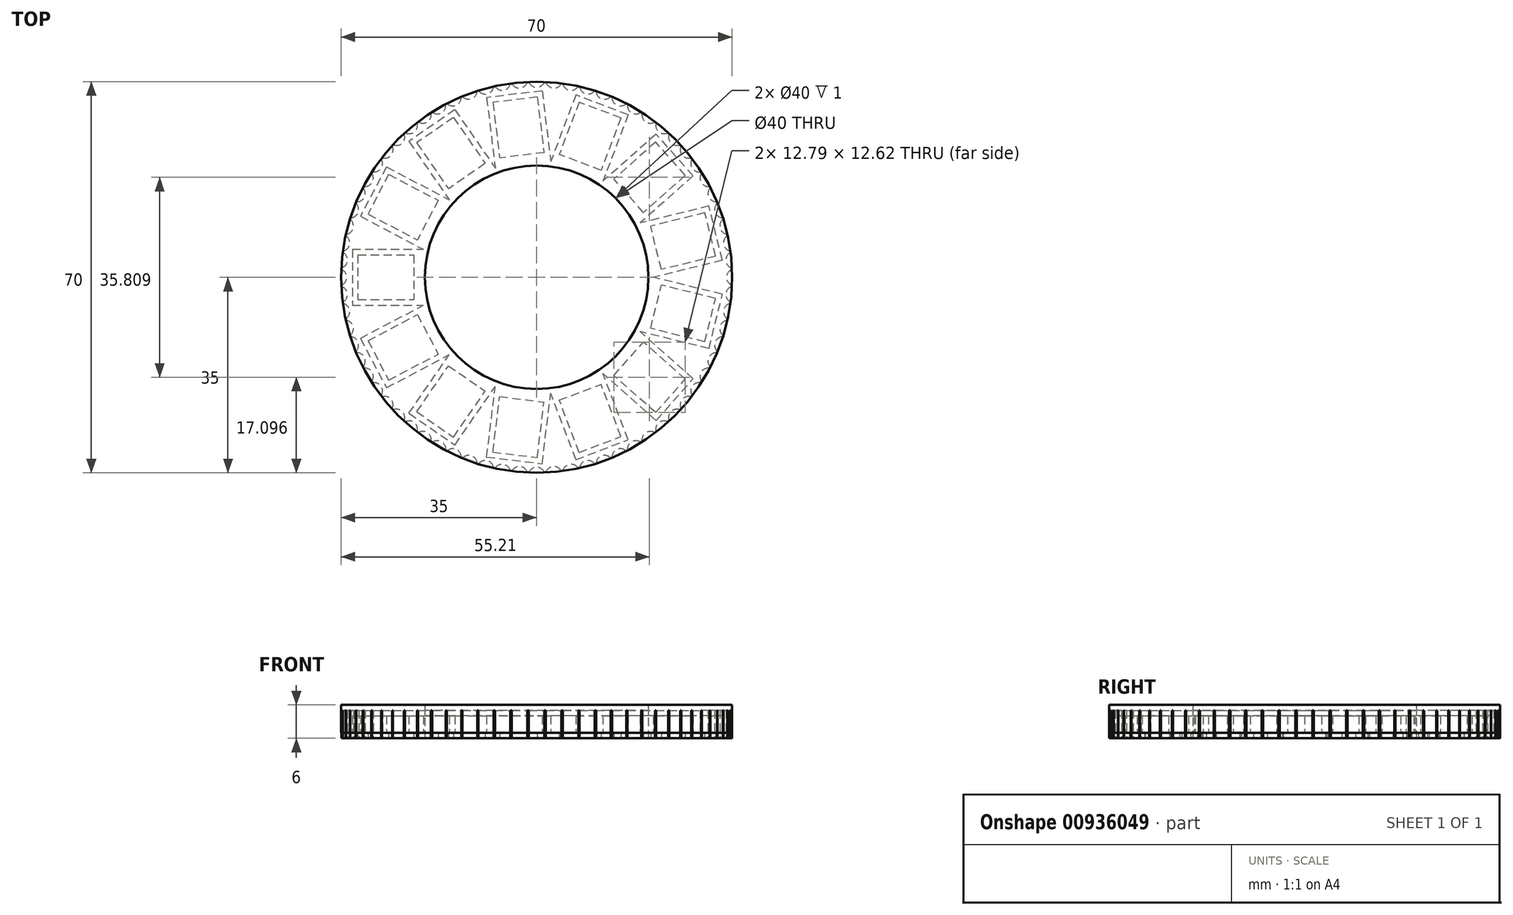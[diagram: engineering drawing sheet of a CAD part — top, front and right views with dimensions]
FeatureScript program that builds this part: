
annotation { "Feature Type Name" : "Feature", "Feature Type Description" : "" }
export const myFeature = defineFeature(function(context is Context, id is Id, definition is map)
    precondition{}
    {
        {
            var Q0;
            Q0=qCreatedBy(makeId("Top.planeOp"),FACE);
            var sketch = newSketch(context, id + "F0", { "sketchPlane" : qUnion([Q0])});
            skLineSegment(sketch, "E0.bottom", {"start": v(-32, 4) * mm, "end": v(-22, 4) * mm});
            skLineSegment(sketch, "E0.top", {"start": v(-32, -4) * mm, "end": v(-22, -4) * mm});
            skLineSegment(sketch, "E0.left", {"start": v(-32, 4) * mm, "end": v(-32, -4) * mm});
            skLineSegment(sketch, "E0.right", {"start": v(-22, 4) * mm, "end": v(-22, -4) * mm});
            skLineSegment(sketch, "E1", {"start": v(0, 0) * mm, "end": v(-43.95, 0) * mm, "construction": true});
            skLineSegment(sketch, "E2.bottom", {"start": v(-33, 5) * mm, "end": v(0, 5) * mm});
            skLineSegment(sketch, "E2.top", {"start": v(-33, -5) * mm, "end": v(0, -5) * mm});
            skLineSegment(sketch, "E2.left", {"start": v(-33, 5) * mm, "end": v(-33, -5) * mm});
            skLineSegment(sketch, "E2.right", {"start": v(0, 5) * mm, "end": v(0, -5) * mm});
            skLineSegment(sketch, "E3.1.0", {"start": v(-30.2, -11.33) * mm, "end": v(-21.34, -6.68) * mm});
            skLineSegment(sketch, "E3.1.1", {"start": v(-26.48, -18.41) * mm, "end": v(-17.62, -13.77) * mm});
            skLineSegment(sketch, "E3.1.2", {"start": v(-30.2, -11.33) * mm, "end": v(-26.48, -18.41) * mm});
            skLineSegment(sketch, "E3.1.3", {"start": v(-31.54, -10.9) * mm, "end": v(-2.32, 4.43) * mm});
            skLineSegment(sketch, "E3.1.4", {"start": v(-21.34, -6.68) * mm, "end": v(-17.62, -13.77) * mm});
            skLineSegment(sketch, "E3.1.5", {"start": v(-26.9, -19.76) * mm, "end": v(2.32, -4.43) * mm});
            skLineSegment(sketch, "E3.1.6", {"start": v(-31.54, -10.9) * mm, "end": v(-26.9, -19.76) * mm});
            skLineSegment(sketch, "E3.1.7", {"start": v(-2.32, 4.43) * mm, "end": v(2.32, -4.43) * mm});
            skLineSegment(sketch, "E3.1.8", {"start": v(0, 0) * mm, "end": v(-38.92, -20.43) * mm, "construction": true});
            skLineSegment(sketch, "E3.2.0", {"start": v(-21.47, -24.06) * mm, "end": v(-15.79, -15.83) * mm});
            skLineSegment(sketch, "E3.2.1", {"start": v(-14.89, -28.6) * mm, "end": v(-9.2, -20.38) * mm});
            skLineSegment(sketch, "E3.2.2", {"start": v(-21.47, -24.06) * mm, "end": v(-14.89, -28.6) * mm});
            skLineSegment(sketch, "E3.2.3", {"start": v(-22.86, -24.32) * mm, "end": v(-4.11, 2.84) * mm});
            skLineSegment(sketch, "E3.2.4", {"start": v(-15.79, -15.83) * mm, "end": v(-9.2, -20.38) * mm});
            skLineSegment(sketch, "E3.2.5", {"start": v(-14.63, -30) * mm, "end": v(4.11, -2.84) * mm});
            skLineSegment(sketch, "E3.2.6", {"start": v(-22.86, -24.32) * mm, "end": v(-14.63, -30) * mm});
            skLineSegment(sketch, "E3.2.7", {"start": v(-4.11, 2.84) * mm, "end": v(4.11, -2.84) * mm});
            skLineSegment(sketch, "E3.2.8", {"start": v(0, 0) * mm, "end": v(-24.97, -36.17) * mm, "construction": true});
            skLineSegment(sketch, "E3.3.0", {"start": v(-7.83, -31.28) * mm, "end": v(-6.62, -21.36) * mm});
            skLineSegment(sketch, "E3.3.1", {"start": v(0.11, -32.25) * mm, "end": v(1.32, -22.32) * mm});
            skLineSegment(sketch, "E3.3.2", {"start": v(-7.83, -31.28) * mm, "end": v(0.11, -32.25) * mm});
            skLineSegment(sketch, "E3.3.3", {"start": v(-8.94, -32.16) * mm, "end": v(-4.96, 0.6) * mm});
            skLineSegment(sketch, "E3.3.4", {"start": v(-6.62, -21.36) * mm, "end": v(1.32, -22.32) * mm});
            skLineSegment(sketch, "E3.3.5", {"start": v(0.99, -33.36) * mm, "end": v(4.96, -0.6) * mm});
            skLineSegment(sketch, "E3.3.6", {"start": v(-8.94, -32.16) * mm, "end": v(0.99, -33.36) * mm});
            skLineSegment(sketch, "E3.3.7", {"start": v(-4.96, 0.6) * mm, "end": v(4.96, -0.6) * mm});
            skLineSegment(sketch, "E3.3.8", {"start": v(0, 0) * mm, "end": v(-5.3, -43.63) * mm, "construction": true});
            skLineSegment(sketch, "E3.4.0", {"start": v(7.6, -31.34) * mm, "end": v(4.06, -21.99) * mm});
            skLineSegment(sketch, "E3.4.1", {"start": v(15.09, -28.5) * mm, "end": v(11.54, -19.15) * mm});
            skLineSegment(sketch, "E3.4.2", {"start": v(7.6, -31.34) * mm, "end": v(15.09, -28.5) * mm});
            skLineSegment(sketch, "E3.4.3", {"start": v(7.03, -32.63) * mm, "end": v(-4.68, -1.77) * mm});
            skLineSegment(sketch, "E3.4.4", {"start": v(4.06, -21.99) * mm, "end": v(11.54, -19.15) * mm});
            skLineSegment(sketch, "E3.4.5", {"start": v(16.38, -29.08) * mm, "end": v(4.68, 1.77) * mm});
            skLineSegment(sketch, "E3.4.6", {"start": v(7.03, -32.63) * mm, "end": v(16.38, -29.08) * mm});
            skLineSegment(sketch, "E3.4.7", {"start": v(-4.68, -1.77) * mm, "end": v(4.68, 1.77) * mm});
            skLineSegment(sketch, "E3.4.8", {"start": v(0, 0) * mm, "end": v(15.59, -41.1) * mm, "construction": true});
            skLineSegment(sketch, "E3.5.0", {"start": v(21.3, -24.21) * mm, "end": v(13.81, -17.58) * mm});
            skLineSegment(sketch, "E3.5.1", {"start": v(26.6, -18.23) * mm, "end": v(19.12, -11.6) * mm});
            skLineSegment(sketch, "E3.5.2", {"start": v(21.3, -24.21) * mm, "end": v(26.6, -18.23) * mm});
            skLineSegment(sketch, "E3.5.3", {"start": v(21.39, -25.63) * mm, "end": v(-3.32, -3.74) * mm});
            skLineSegment(sketch, "E3.5.4", {"start": v(13.81, -17.58) * mm, "end": v(19.12, -11.6) * mm});
            skLineSegment(sketch, "E3.5.5", {"start": v(28.02, -18.14) * mm, "end": v(3.32, 3.74) * mm});
            skLineSegment(sketch, "E3.5.6", {"start": v(21.39, -25.63) * mm, "end": v(28.02, -18.14) * mm});
            skLineSegment(sketch, "E3.5.7", {"start": v(-3.32, -3.74) * mm, "end": v(3.32, 3.74) * mm});
            skLineSegment(sketch, "E3.5.8", {"start": v(0, 0) * mm, "end": v(32.9, -29.15) * mm, "construction": true});
            skLineSegment(sketch, "E3.6.0", {"start": v(30.11, -11.54) * mm, "end": v(20.4, -9.15) * mm});
            skLineSegment(sketch, "E3.6.1", {"start": v(32.03, -3.77) * mm, "end": v(22.32, -1.38) * mm});
            skLineSegment(sketch, "E3.6.2", {"start": v(30.11, -11.54) * mm, "end": v(32.03, -3.77) * mm});
            skLineSegment(sketch, "E3.6.3", {"start": v(30.84, -12.75) * mm, "end": v(-1.2, -4.85) * mm});
            skLineSegment(sketch, "E3.6.4", {"start": v(20.4, -9.15) * mm, "end": v(22.32, -1.38) * mm});
            skLineSegment(sketch, "E3.6.5", {"start": v(33.24, -3.04) * mm, "end": v(1.2, 4.85) * mm});
            skLineSegment(sketch, "E3.6.6", {"start": v(30.84, -12.75) * mm, "end": v(33.24, -3.04) * mm});
            skLineSegment(sketch, "E3.6.7", {"start": v(-1.2, -4.85) * mm, "end": v(1.2, 4.85) * mm});
            skLineSegment(sketch, "E3.6.8", {"start": v(0, 0) * mm, "end": v(42.68, -10.52) * mm, "construction": true});
            skLineSegment(sketch, "E3.7.0", {"start": v(32.03, 3.77) * mm, "end": v(22.32, 1.38) * mm});
            skLineSegment(sketch, "E3.7.1", {"start": v(30.11, 11.54) * mm, "end": v(20.4, 9.15) * mm});
            skLineSegment(sketch, "E3.7.2", {"start": v(32.03, 3.77) * mm, "end": v(30.11, 11.54) * mm});
            skLineSegment(sketch, "E3.7.3", {"start": v(33.24, 3.04) * mm, "end": v(1.2, -4.85) * mm});
            skLineSegment(sketch, "E3.7.4", {"start": v(22.32, 1.38) * mm, "end": v(20.4, 9.15) * mm});
            skLineSegment(sketch, "E3.7.5", {"start": v(30.84, 12.75) * mm, "end": v(-1.2, 4.85) * mm});
            skLineSegment(sketch, "E3.7.6", {"start": v(33.24, 3.04) * mm, "end": v(30.84, 12.75) * mm});
            skLineSegment(sketch, "E3.7.7", {"start": v(1.2, -4.85) * mm, "end": v(-1.2, 4.85) * mm});
            skLineSegment(sketch, "E3.7.8", {"start": v(0, 0) * mm, "end": v(42.68, 10.52) * mm, "construction": true});
            skLineSegment(sketch, "E3.8.0", {"start": v(26.6, 18.23) * mm, "end": v(19.12, 11.6) * mm});
            skLineSegment(sketch, "E3.8.1", {"start": v(21.3, 24.21) * mm, "end": v(13.81, 17.58) * mm});
            skLineSegment(sketch, "E3.8.2", {"start": v(26.6, 18.23) * mm, "end": v(21.3, 24.21) * mm});
            skLineSegment(sketch, "E3.8.3", {"start": v(28.02, 18.14) * mm, "end": v(3.32, -3.74) * mm});
            skLineSegment(sketch, "E3.8.4", {"start": v(19.12, 11.6) * mm, "end": v(13.81, 17.58) * mm});
            skLineSegment(sketch, "E3.8.5", {"start": v(21.39, 25.63) * mm, "end": v(-3.32, 3.74) * mm});
            skLineSegment(sketch, "E3.8.6", {"start": v(28.02, 18.14) * mm, "end": v(21.39, 25.63) * mm});
            skLineSegment(sketch, "E3.8.7", {"start": v(3.32, -3.74) * mm, "end": v(-3.32, 3.74) * mm});
            skLineSegment(sketch, "E3.8.8", {"start": v(0, 0) * mm, "end": v(32.9, 29.15) * mm, "construction": true});
            skLineSegment(sketch, "E3.9.0", {"start": v(15.09, 28.5) * mm, "end": v(11.54, 19.15) * mm});
            skLineSegment(sketch, "E3.9.1", {"start": v(7.6, 31.34) * mm, "end": v(4.06, 21.99) * mm});
            skLineSegment(sketch, "E3.9.2", {"start": v(15.09, 28.5) * mm, "end": v(7.6, 31.34) * mm});
            skLineSegment(sketch, "E3.9.3", {"start": v(16.38, 29.08) * mm, "end": v(4.68, -1.77) * mm});
            skLineSegment(sketch, "E3.9.4", {"start": v(11.54, 19.15) * mm, "end": v(4.06, 21.99) * mm});
            skLineSegment(sketch, "E3.9.5", {"start": v(7.03, 32.63) * mm, "end": v(-4.68, 1.77) * mm});
            skLineSegment(sketch, "E3.9.6", {"start": v(16.38, 29.08) * mm, "end": v(7.03, 32.63) * mm});
            skLineSegment(sketch, "E3.9.7", {"start": v(4.68, -1.77) * mm, "end": v(-4.68, 1.77) * mm});
            skLineSegment(sketch, "E3.9.8", {"start": v(0, 0) * mm, "end": v(15.59, 41.1) * mm, "construction": true});
            skLineSegment(sketch, "E3.10.0", {"start": v(0.11, 32.25) * mm, "end": v(1.32, 22.32) * mm});
            skLineSegment(sketch, "E3.10.1", {"start": v(-7.83, 31.28) * mm, "end": v(-6.62, 21.36) * mm});
            skLineSegment(sketch, "E3.10.2", {"start": v(0.11, 32.25) * mm, "end": v(-7.83, 31.28) * mm});
            skLineSegment(sketch, "E3.10.3", {"start": v(0.99, 33.36) * mm, "end": v(4.96, 0.6) * mm});
            skLineSegment(sketch, "E3.10.4", {"start": v(1.32, 22.32) * mm, "end": v(-6.62, 21.36) * mm});
            skLineSegment(sketch, "E3.10.5", {"start": v(-8.94, 32.16) * mm, "end": v(-4.96, -0.6) * mm});
            skLineSegment(sketch, "E3.10.6", {"start": v(0.99, 33.36) * mm, "end": v(-8.94, 32.16) * mm});
            skLineSegment(sketch, "E3.10.7", {"start": v(4.96, 0.6) * mm, "end": v(-4.96, -0.6) * mm});
            skLineSegment(sketch, "E3.10.8", {"start": v(0, 0) * mm, "end": v(-5.3, 43.63) * mm, "construction": true});
            skLineSegment(sketch, "E3.11.0", {"start": v(-14.89, 28.6) * mm, "end": v(-9.2, 20.38) * mm});
            skLineSegment(sketch, "E3.11.1", {"start": v(-21.47, 24.06) * mm, "end": v(-15.79, 15.83) * mm});
            skLineSegment(sketch, "E3.11.2", {"start": v(-14.89, 28.6) * mm, "end": v(-21.47, 24.06) * mm});
            skLineSegment(sketch, "E3.11.3", {"start": v(-14.63, 30) * mm, "end": v(4.11, 2.84) * mm});
            skLineSegment(sketch, "E3.11.4", {"start": v(-9.2, 20.38) * mm, "end": v(-15.79, 15.83) * mm});
            skLineSegment(sketch, "E3.11.5", {"start": v(-22.86, 24.32) * mm, "end": v(-4.11, -2.84) * mm});
            skLineSegment(sketch, "E3.11.6", {"start": v(-14.63, 30) * mm, "end": v(-22.86, 24.32) * mm});
            skLineSegment(sketch, "E3.11.7", {"start": v(4.11, 2.84) * mm, "end": v(-4.11, -2.84) * mm});
            skLineSegment(sketch, "E3.11.8", {"start": v(0, 0) * mm, "end": v(-24.97, 36.17) * mm, "construction": true});
            skLineSegment(sketch, "E3.12.0", {"start": v(-26.48, 18.41) * mm, "end": v(-17.62, 13.77) * mm});
            skLineSegment(sketch, "E3.12.1", {"start": v(-30.2, 11.33) * mm, "end": v(-21.34, 6.68) * mm});
            skLineSegment(sketch, "E3.12.2", {"start": v(-26.48, 18.41) * mm, "end": v(-30.2, 11.33) * mm});
            skLineSegment(sketch, "E3.12.3", {"start": v(-26.9, 19.76) * mm, "end": v(2.32, 4.43) * mm});
            skLineSegment(sketch, "E3.12.4", {"start": v(-17.62, 13.77) * mm, "end": v(-21.34, 6.68) * mm});
            skLineSegment(sketch, "E3.12.5", {"start": v(-31.54, 10.9) * mm, "end": v(-2.32, -4.43) * mm});
            skLineSegment(sketch, "E3.12.6", {"start": v(-26.9, 19.76) * mm, "end": v(-31.54, 10.9) * mm});
            skLineSegment(sketch, "E3.12.7", {"start": v(2.32, 4.43) * mm, "end": v(-2.32, -4.43) * mm});
            skLineSegment(sketch, "E3.12.8", {"start": v(0, 0) * mm, "end": v(-38.92, 20.43) * mm, "construction": true});
            skPoint(sketch, "E3.center", {"position": v(0, 0) * mm});
            skSolve(sketch);
        }
        {
            var Q0;
            Q0=qCreatedBy(makeId("Top.planeOp"),FACE);
            var sketch = newSketch(context, id + "F1", { "sketchPlane" : qUnion([Q0])});
            skCircle(sketch, "E4", {"center": v(0, 0) * mm, "radius": 35 * mm});
            skCircle(sketch, "E5", {"center": v(0, 0) * mm, "radius": 20 * mm});
            skSolve(sketch);
        }
        {
            var Q0;
            Q0 = qSketchRegion(id + "F1", true);
            extrude(context, id + "F2", {"entities" : qUnion([Q0]), "depth" : 4 * mm, "offsetDistance" : 25 * mm, "hasSecondDirection" : true, "secondDirectionOppositeDirection" : true, "secondDirectionDepth" : 1 * mm});
        }
        {
            var Q0;
            Q0=makeQuery(id+"F0.imprint","IMPRINT",FACE,{"disambiguationData":[TD([[makeQuery(id+"F0.imprint","IMPRINT",EDGE,{"derivedFrom":sQuery(id+"F0.wireOp",EDGE,"E0.bottom")}),-1.0]])]});
            var Q1;
            Q1=makeQuery(id+"F0.imprint","IMPRINT",FACE,{"disambiguationData":[TD([[makeQuery(id+"F0.imprint","IMPRINT",EDGE,{"derivedFrom":sQuery(id+"F0.wireOp",EDGE,"E3.1.0")}),-1.0]])]});
            var Q2;
            Q2=makeQuery(id+"F0.imprint","IMPRINT",FACE,{"disambiguationData":[TD([[makeQuery(id+"F0.imprint","IMPRINT",EDGE,{"derivedFrom":sQuery(id+"F0.wireOp",EDGE,"E3.2.0")}),-1.0]])]});
            var Q3;
            Q3=makeQuery(id+"F0.imprint","IMPRINT",FACE,{"disambiguationData":[TD([[makeQuery(id+"F0.imprint","IMPRINT",EDGE,{"derivedFrom":sQuery(id+"F0.wireOp",EDGE,"E3.3.0")}),-1.0]])]});
            var Q4;
            Q4=makeQuery(id+"F0.imprint","IMPRINT",FACE,{"disambiguationData":[TD([[makeQuery(id+"F0.imprint","IMPRINT",EDGE,{"derivedFrom":sQuery(id+"F0.wireOp",EDGE,"E3.4.0")}),-1.0]])]});
            var Q5;
            Q5=makeQuery(id+"F0.imprint","IMPRINT",FACE,{"disambiguationData":[TD([[makeQuery(id+"F0.imprint","IMPRINT",EDGE,{"derivedFrom":sQuery(id+"F0.wireOp",EDGE,"E3.5.0")}),-1.0]])]});
            var Q6;
            Q6=makeQuery(id+"F0.imprint","IMPRINT",FACE,{"disambiguationData":[TD([[makeQuery(id+"F0.imprint","IMPRINT",EDGE,{"derivedFrom":sQuery(id+"F0.wireOp",EDGE,"E3.6.0")}),-1.0]])]});
            var Q7;
            Q7=makeQuery(id+"F0.imprint","IMPRINT",FACE,{"disambiguationData":[TD([[makeQuery(id+"F0.imprint","IMPRINT",EDGE,{"derivedFrom":sQuery(id+"F0.wireOp",EDGE,"E3.7.0")}),-1.0]])]});
            var Q8;
            Q8=makeQuery(id+"F0.imprint","IMPRINT",FACE,{"disambiguationData":[TD([[makeQuery(id+"F0.imprint","IMPRINT",EDGE,{"derivedFrom":sQuery(id+"F0.wireOp",EDGE,"E3.8.0")}),-1.0]])]});
            var Q9;
            Q9=makeQuery(id+"F0.imprint","IMPRINT",FACE,{"disambiguationData":[TD([[makeQuery(id+"F0.imprint","IMPRINT",EDGE,{"derivedFrom":sQuery(id+"F0.wireOp",EDGE,"E3.9.0")}),-1.0]])]});
            var Q10;
            Q10=makeQuery(id+"F0.imprint","IMPRINT",FACE,{"disambiguationData":[TD([[makeQuery(id+"F0.imprint","IMPRINT",EDGE,{"derivedFrom":sQuery(id+"F0.wireOp",EDGE,"E3.10.0")}),-1.0]])]});
            var Q11;
            Q11=makeQuery(id+"F0.imprint","IMPRINT",FACE,{"disambiguationData":[TD([[makeQuery(id+"F0.imprint","IMPRINT",EDGE,{"derivedFrom":sQuery(id+"F0.wireOp",EDGE,"E3.11.0")}),-1.0]])]});
            var Q12;
            Q12=makeQuery(id+"F0.imprint","IMPRINT",FACE,{"disambiguationData":[TD([[makeQuery(id+"F0.imprint","IMPRINT",EDGE,{"derivedFrom":sQuery(id+"F0.wireOp",EDGE,"E3.12.0")}),-1.0]])]});
            extrude(context, id + "F3", {"entities" : qUnion([Q0, Q1, Q2, Q3, Q4, Q5, Q6, Q7, Q8, Q9, Q10, Q11, Q12]), "operationType" : NewBodyOperationType.REMOVE, "depth" : 3 * mm, "offsetDistance" : 25 * mm, "hasSecondDirection" : true, "secondDirectionOppositeDirection" : true, "secondDirectionDepth" : 1 * mm});
        }
        {
            var Q0;
            Q0 = qSketchRegion(id + "F0", true);
            extrude(context, id + "F4", {"entities" : qUnion([Q0]), "operationType" : NewBodyOperationType.REMOVE, "depth" : 3 * mm, "offsetDistance" : 25 * mm});
        }
        {
            var Q0;
            Q0=qCreatedBy(makeId("Top.planeOp"),FACE);
            var sketch = newSketch(context, id + "F5", { "sketchPlane" : qUnion([Q0])});
            skCircle(sketch, "E6", {"center": v(-35.5, 0) * mm, "radius": 1.5 * mm});
            skCircle(sketch, "E7.1.0", {"center": v(-35.36, -3.1) * mm, "radius": 1.5 * mm});
            skCircle(sketch, "E7.2.0", {"center": v(-34.96, -6.16) * mm, "radius": 1.5 * mm});
            skCircle(sketch, "E7.3.0", {"center": v(-34.3, -9.19) * mm, "radius": 1.5 * mm});
            skCircle(sketch, "E7.4.0", {"center": v(-33.36, -12.14) * mm, "radius": 1.5 * mm});
            skCircle(sketch, "E7.5.0", {"center": v(-32.17, -15) * mm, "radius": 1.5 * mm});
            skCircle(sketch, "E7.6.0", {"center": v(-30.74, -17.75) * mm, "radius": 1.5 * mm});
            skCircle(sketch, "E7.7.0", {"center": v(-29.08, -20.36) * mm, "radius": 1.5 * mm});
            skCircle(sketch, "E7.8.0", {"center": v(-27.2, -22.82) * mm, "radius": 1.5 * mm});
            skCircle(sketch, "E7.9.0", {"center": v(-25.1, -25.1) * mm, "radius": 1.5 * mm});
            skCircle(sketch, "E7.10.0", {"center": v(-22.82, -27.2) * mm, "radius": 1.5 * mm});
            skCircle(sketch, "E7.11.0", {"center": v(-20.36, -29.08) * mm, "radius": 1.5 * mm});
            skCircle(sketch, "E7.12.0", {"center": v(-17.75, -30.74) * mm, "radius": 1.5 * mm});
            skCircle(sketch, "E7.13.0", {"center": v(-15, -32.17) * mm, "radius": 1.5 * mm});
            skCircle(sketch, "E7.14.0", {"center": v(-12.14, -33.36) * mm, "radius": 1.5 * mm});
            skCircle(sketch, "E7.15.0", {"center": v(-9.19, -34.3) * mm, "radius": 1.5 * mm});
            skCircle(sketch, "E7.16.0", {"center": v(-6.16, -34.96) * mm, "radius": 1.5 * mm});
            skCircle(sketch, "E7.17.0", {"center": v(-3.1, -35.36) * mm, "radius": 1.5 * mm});
            skCircle(sketch, "E7.18.0", {"center": v(0, -35.5) * mm, "radius": 1.5 * mm});
            skCircle(sketch, "E7.19.0", {"center": v(3.1, -35.36) * mm, "radius": 1.5 * mm});
            skCircle(sketch, "E7.20.0", {"center": v(6.16, -34.96) * mm, "radius": 1.5 * mm});
            skCircle(sketch, "E7.21.0", {"center": v(9.19, -34.3) * mm, "radius": 1.5 * mm});
            skCircle(sketch, "E7.22.0", {"center": v(12.14, -33.36) * mm, "radius": 1.5 * mm});
            skCircle(sketch, "E7.23.0", {"center": v(15, -32.17) * mm, "radius": 1.5 * mm});
            skCircle(sketch, "E7.24.0", {"center": v(17.75, -30.74) * mm, "radius": 1.5 * mm});
            skCircle(sketch, "E7.25.0", {"center": v(20.36, -29.08) * mm, "radius": 1.5 * mm});
            skCircle(sketch, "E7.26.0", {"center": v(22.82, -27.2) * mm, "radius": 1.5 * mm});
            skCircle(sketch, "E7.27.0", {"center": v(25.1, -25.1) * mm, "radius": 1.5 * mm});
            skCircle(sketch, "E7.28.0", {"center": v(27.2, -22.82) * mm, "radius": 1.5 * mm});
            skCircle(sketch, "E7.29.0", {"center": v(29.08, -20.36) * mm, "radius": 1.5 * mm});
            skCircle(sketch, "E7.30.0", {"center": v(30.74, -17.75) * mm, "radius": 1.5 * mm});
            skCircle(sketch, "E7.31.0", {"center": v(32.17, -15) * mm, "radius": 1.5 * mm});
            skCircle(sketch, "E7.32.0", {"center": v(33.36, -12.14) * mm, "radius": 1.5 * mm});
            skCircle(sketch, "E7.33.0", {"center": v(34.3, -9.19) * mm, "radius": 1.5 * mm});
            skCircle(sketch, "E7.34.0", {"center": v(34.96, -6.16) * mm, "radius": 1.5 * mm});
            skCircle(sketch, "E7.35.0", {"center": v(35.36, -3.1) * mm, "radius": 1.5 * mm});
            skCircle(sketch, "E7.36.0", {"center": v(35.5, 0) * mm, "radius": 1.5 * mm});
            skCircle(sketch, "E7.37.0", {"center": v(35.36, 3.1) * mm, "radius": 1.5 * mm});
            skCircle(sketch, "E7.38.0", {"center": v(34.96, 6.16) * mm, "radius": 1.5 * mm});
            skCircle(sketch, "E7.39.0", {"center": v(34.3, 9.19) * mm, "radius": 1.5 * mm});
            skCircle(sketch, "E7.40.0", {"center": v(33.36, 12.14) * mm, "radius": 1.5 * mm});
            skCircle(sketch, "E7.41.0", {"center": v(32.17, 15) * mm, "radius": 1.5 * mm});
            skCircle(sketch, "E7.42.0", {"center": v(30.74, 17.75) * mm, "radius": 1.5 * mm});
            skCircle(sketch, "E7.43.0", {"center": v(29.08, 20.36) * mm, "radius": 1.5 * mm});
            skCircle(sketch, "E7.44.0", {"center": v(27.2, 22.82) * mm, "radius": 1.5 * mm});
            skCircle(sketch, "E7.45.0", {"center": v(25.1, 25.1) * mm, "radius": 1.5 * mm});
            skCircle(sketch, "E7.46.0", {"center": v(22.82, 27.2) * mm, "radius": 1.5 * mm});
            skCircle(sketch, "E7.47.0", {"center": v(20.36, 29.08) * mm, "radius": 1.5 * mm});
            skCircle(sketch, "E7.48.0", {"center": v(17.75, 30.74) * mm, "radius": 1.5 * mm});
            skCircle(sketch, "E7.49.0", {"center": v(15, 32.17) * mm, "radius": 1.5 * mm});
            skCircle(sketch, "E7.50.0", {"center": v(12.14, 33.36) * mm, "radius": 1.5 * mm});
            skCircle(sketch, "E7.51.0", {"center": v(9.19, 34.3) * mm, "radius": 1.5 * mm});
            skCircle(sketch, "E7.52.0", {"center": v(6.16, 34.96) * mm, "radius": 1.5 * mm});
            skCircle(sketch, "E7.53.0", {"center": v(3.1, 35.36) * mm, "radius": 1.5 * mm});
            skCircle(sketch, "E7.54.0", {"center": v(0, 35.5) * mm, "radius": 1.5 * mm});
            skCircle(sketch, "E7.55.0", {"center": v(-3.1, 35.36) * mm, "radius": 1.5 * mm});
            skCircle(sketch, "E7.56.0", {"center": v(-6.16, 34.96) * mm, "radius": 1.5 * mm});
            skCircle(sketch, "E7.57.0", {"center": v(-9.19, 34.3) * mm, "radius": 1.5 * mm});
            skCircle(sketch, "E7.58.0", {"center": v(-12.14, 33.36) * mm, "radius": 1.5 * mm});
            skCircle(sketch, "E7.59.0", {"center": v(-15, 32.17) * mm, "radius": 1.5 * mm});
            skCircle(sketch, "E7.60.0", {"center": v(-17.75, 30.74) * mm, "radius": 1.5 * mm});
            skCircle(sketch, "E7.61.0", {"center": v(-20.36, 29.08) * mm, "radius": 1.5 * mm});
            skCircle(sketch, "E7.62.0", {"center": v(-22.82, 27.2) * mm, "radius": 1.5 * mm});
            skCircle(sketch, "E7.63.0", {"center": v(-25.1, 25.1) * mm, "radius": 1.5 * mm});
            skCircle(sketch, "E7.64.0", {"center": v(-27.2, 22.82) * mm, "radius": 1.5 * mm});
            skCircle(sketch, "E7.65.0", {"center": v(-29.08, 20.36) * mm, "radius": 1.5 * mm});
            skCircle(sketch, "E7.66.0", {"center": v(-30.74, 17.75) * mm, "radius": 1.5 * mm});
            skCircle(sketch, "E7.67.0", {"center": v(-32.17, 15) * mm, "radius": 1.5 * mm});
            skCircle(sketch, "E7.68.0", {"center": v(-33.36, 12.14) * mm, "radius": 1.5 * mm});
            skCircle(sketch, "E7.69.0", {"center": v(-34.3, 9.19) * mm, "radius": 1.5 * mm});
            skCircle(sketch, "E7.70.0", {"center": v(-34.96, 6.16) * mm, "radius": 1.5 * mm});
            skCircle(sketch, "E7.71.0", {"center": v(-35.36, 3.1) * mm, "radius": 1.5 * mm});
            skPoint(sketch, "E7.center", {"position": v(0, 0) * mm});
            skSolve(sketch);
        }
        {
            var Q0;
            Q0 = qSketchRegion(id + "F5", true);
            extrude(context, id + "F6", {"entities" : qUnion([Q0]), "operationType" : NewBodyOperationType.REMOVE, "endBound" : BoundingType.THROUGH_ALL, "depth" : 25 * mm, "offsetDistance" : 25 * mm, "hasSecondDirection" : true, "secondDirectionBound" : SecondDirectionBoundingType.THROUGH_ALL, "secondDirectionOppositeDirection" : true, "secondDirectionDepth" : 25 * mm});
        }
        {
            var Q0;
            Q0=makeQuery(id+"F1.imprint","IMPRINT",FACE,{"disambiguationData":[TD([[makeQuery(id+"F1.imprint","IMPRINT",EDGE,{"derivedFrom":sQuery(id+"F1.wireOp",EDGE,"E4")}),1.0]])]});
            extrude(context, id + "F7", {"entities" : qUnion([Q0]), "depth" : 5 * mm, "offsetDistance" : 25 * mm});
        }
    });
